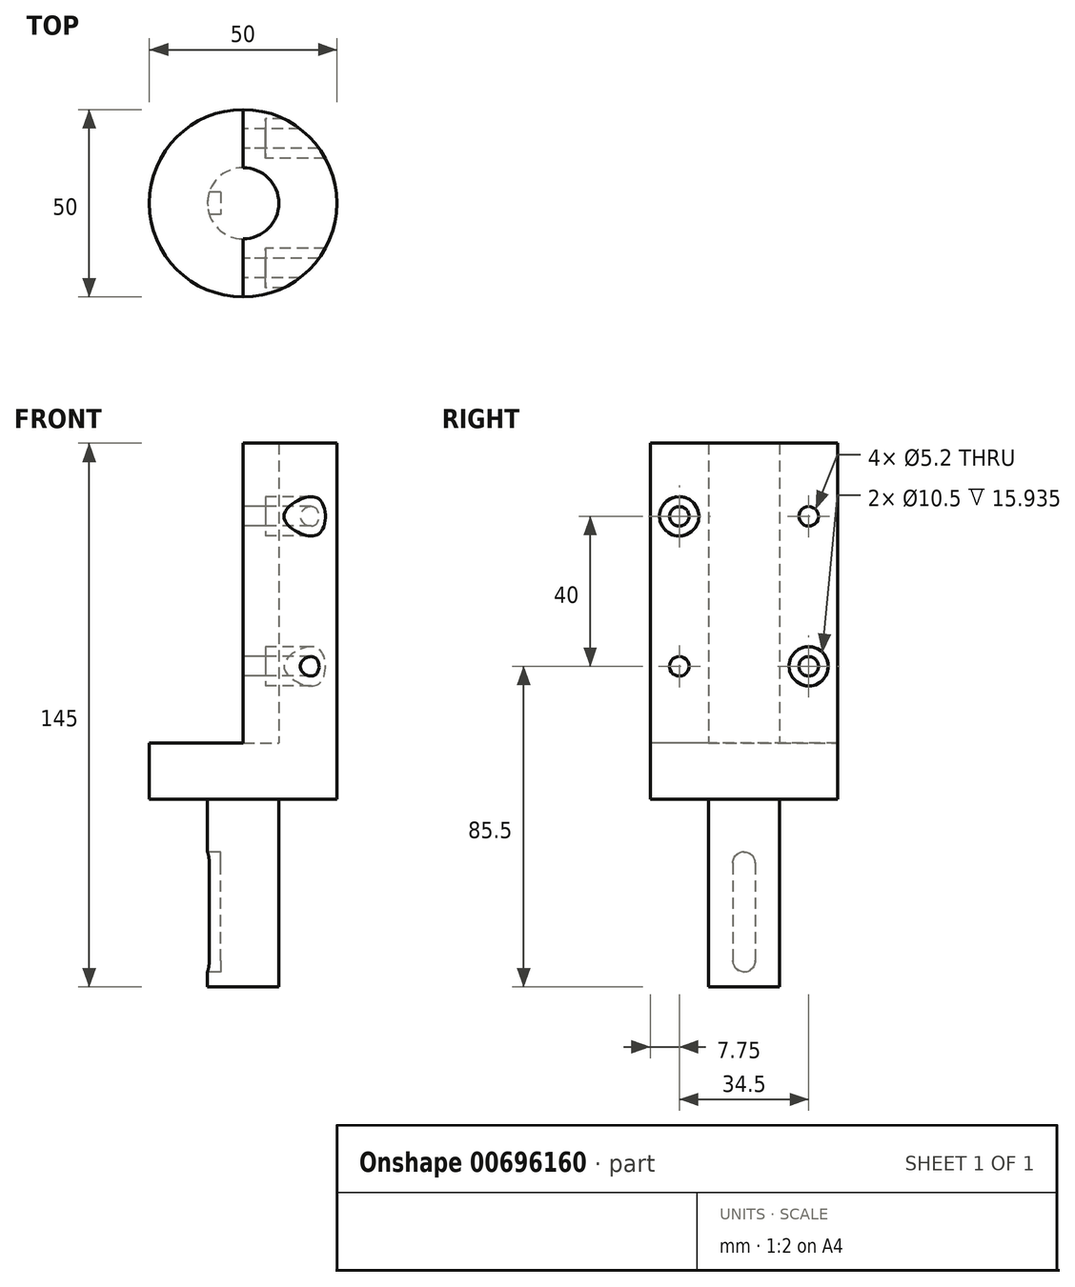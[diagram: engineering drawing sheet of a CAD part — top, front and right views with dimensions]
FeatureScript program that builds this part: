
annotation { "Feature Type Name" : "Feature", "Feature Type Description" : "" }
export const myFeature = defineFeature(function(context is Context, id is Id, definition is map)
    precondition{}
    {
        {
            var Q0;
            Q0=qCreatedBy(makeId("Top.planeOp"),FACE);
            var sketch = newSketch(context, id + "F0", { "sketchPlane" : qUnion([Q0])});
            skCircle(sketch, "E0", {"center": v(0, 0) * mm, "radius": 9.5 * mm});
            skSolve(sketch);
        }
        {
            var Q0;
            Q0=qSketchRegion(id+"F0",true);
            extrude(context, id + "F1", {"entities" : qUnion([Q0]), "depth" : 50 * mm});
        }
        {
            var Q0;
            Q0=makeQuery(id+"F1.opExtrude","CAP_FACE",FACE,{"disambiguationData":[OSD([sQuery(id+"F0.wireOp",EDGE,"E0")])],"isStart":false});
            var sketch = newSketch(context, id + "F2", { "sketchPlane" : qUnion([Q0])});
            skCircle(sketch, "E1", {"center": v(0, 0) * mm, "radius": 25 * mm});
            skSolve(sketch);
        }
        {
            var Q0;
            Q0=qSketchRegion(id+"F2",true);
            extrude(context, id + "F3", {"entities" : qUnion([Q0]), "operationType" : NewBodyOperationType.ADD, "depth" : 15 * mm, "offsetDistance" : 25 * mm});
        }
        {
            var Q0;
            Q0=makeQuery(id+"F3.opExtrude","CAP_FACE",FACE,{"disambiguationData":[OSD([sQuery(id+"F2.wireOp",EDGE,"E1")])],"isStart":false});
            var sketch = newSketch(context, id + "F4", { "sketchPlane" : qUnion([Q0])});
            skArc(sketch, "E2", {"start": v(0, -9.5) * mm, "mid": v(9.5, 0) * mm, "end": v(0, 9.5) * mm});
            skArc(sketch, "E3", {"start": v(0, -25) * mm, "mid": v(25, 0) * mm, "end": v(0, 25) * mm});
            skLineSegment(sketch, "E4", {"start": v(0, 9.5) * mm, "end": v(0, 25) * mm});
            skLineSegment(sketch, "E5", {"start": v(0, -9.5) * mm, "end": v(0, -25) * mm});
            skSolve(sketch);
        }
        {
            var Q0;
            Q0=makeQuery(id+"F4.imprint","IMPRINT",FACE,{"disambiguationData":[TD([[makeQuery(id+"F4.imprint","IMPRINT",EDGE,{"derivedFrom":sQuery(id+"F4.wireOp",EDGE,"E2")}),-1.0]])]});
            extrude(context, id + "F5", {"entities" : qUnion([Q0]), "operationType" : NewBodyOperationType.ADD, "depth" : 80 * mm});
        }
        {
            var Q0;
            Q0=makeQuery(id+"F5.opExtrude","SWEPT_FACE",FACE,{"disambiguationData":[OSD([sQuery(id+"F4.wireOp",EDGE,"E5")])]});
            var sketch = newSketch(context, id + "F6", { "sketchPlane" : qUnion([Q0])});
            skCircle(sketch, "E6", {"center": v(17.25, 85.5) * mm, "radius": 2.6 * mm});
            skPoint(sketch, "E6.centerSnap0", {"position": v(17.25, 65) * mm});
            skCircle(sketch, "E7", {"center": v(17.25, 125.5) * mm, "radius": 2.6 * mm});
            skCircle(sketch, "E8", {"center": v(-17.25, 125.5) * mm, "radius": 2.6 * mm});
            skCircle(sketch, "E9", {"center": v(-17.25, 85.5) * mm, "radius": 2.6 * mm});
            skSolve(sketch);
        }
        {
            var Q0;
            Q0=qSketchRegion(id+"F6",true);
            extrude(context, id + "F7", {"entities" : qUnion([Q0]), "operationType" : NewBodyOperationType.REMOVE, "endBound" : BoundingType.THROUGH_ALL, "oppositeDirection" : true, "depth" : 25 * mm});
        }
        {
            var Q0;
            Q0=makeQuery(id+"F5.opExtrude","SWEPT_FACE",FACE,{"disambiguationData":[OSD([sQuery(id+"F4.wireOp",EDGE,"E5")])]});
            cPlane(context, id + "F8", {"entities" : qUnion([Q0]), "cplaneType" : CPlaneType.OFFSET, "offset" : 6 * mm, "oppositeDirection" : true, "width" : 150 * mm, "height" : 150 * mm});
        }
        {
            var Q0;
            Q0=qCreatedBy(id+"F8.planeOp",FACE);
            var sketch = newSketch(context, id + "F9", { "sketchPlane" : qUnion([Q0])});
            skCircle(sketch, "E10", {"center": v(17.25, 125.5) * mm, "radius": 5.25 * mm});
            skLineSegment(sketch, "E11", {"start": v(17.25, 125.5) * mm, "end": v(17.25, 85.5) * mm});
            skLineSegment(sketch, "E12", {"start": v(17.25, 85.5) * mm, "end": v(-17.25, 85.5) * mm});
            skCircle(sketch, "E13", {"center": v(-17.25, 85.5) * mm, "radius": 5.25 * mm});
            skSolve(sketch);
        }
        {
            var Q0;
            Q0=qSketchRegion(id+"F9",true);
            extrude(context, id + "F10", {"entities" : qUnion([Q0]), "operationType" : NewBodyOperationType.REMOVE, "oppositeDirection" : true, "depth" : 25 * mm});
        }
        {
            var Q0;
            Q0=qCreatedBy(makeId("Right.planeOp"),FACE);
            cPlane(context, id + "F11", {"entities" : qUnion([Q0]), "cplaneType" : CPlaneType.OFFSET, "offset" : 9.5 * mm, "oppositeDirection" : true, "width" : 150 * mm, "height" : 150 * mm});
        }
        {
            var Q0;
            Q0=qCreatedBy(id+"F11.planeOp",FACE);
            var sketch = newSketch(context, id + "F12", { "sketchPlane" : qUnion([Q0])});
            skPoint(sketch, "E14.middle", {"position": v(0, 0) * mm});
            skLineSegment(sketch, "E15.left", {"start": v(-3, 7) * mm, "end": v(-3, 33) * mm});
            skLineSegment(sketch, "E15.right", {"start": v(3, 7) * mm, "end": v(3, 33) * mm});
            skArc(sketch, "E16", {"start": v(3, 33) * mm, "mid": v(0, 36) * mm, "end": v(-3, 33) * mm});
            skPoint(sketch, "E16.startSnap0", {"position": v(0, 33) * mm});
            skArc(sketch, "E17", {"start": v(-3, 7) * mm, "mid": v(0, 4) * mm, "end": v(3, 7) * mm});
            skPoint(sketch, "E17.startSnap0", {"position": v(0, 7) * mm});
            skPoint(sketch, "E14.bottom.start.orphan", {"position": v(-3, 4) * mm});
            skSolve(sketch);
        }
        {
            var Q0;
            Q0 = qSketchRegion(id + "F12", true);
            var Q1;
            Q1=sQuery(id+"F12.wireOp",EDGE,"E16");
            var Q2;
            Q2=sQuery(id+"F12.wireOp",EDGE,"E15.right");
            var Q3;
            Q3=sQuery(id+"F12.wireOp",EDGE,"E17");
            var Q4;
            Q4=sQuery(id+"F12.wireOp",EDGE,"E15.left");
            extrude(context, id + "F13", {"entities" : qUnion([Q0]), "operationType" : NewBodyOperationType.REMOVE, "surfaceEntities" : qUnion([Q1, Q2, Q3, Q4]), "depth" : 3.5 * mm, "offsetDistance" : 25 * mm});
        }
    });
